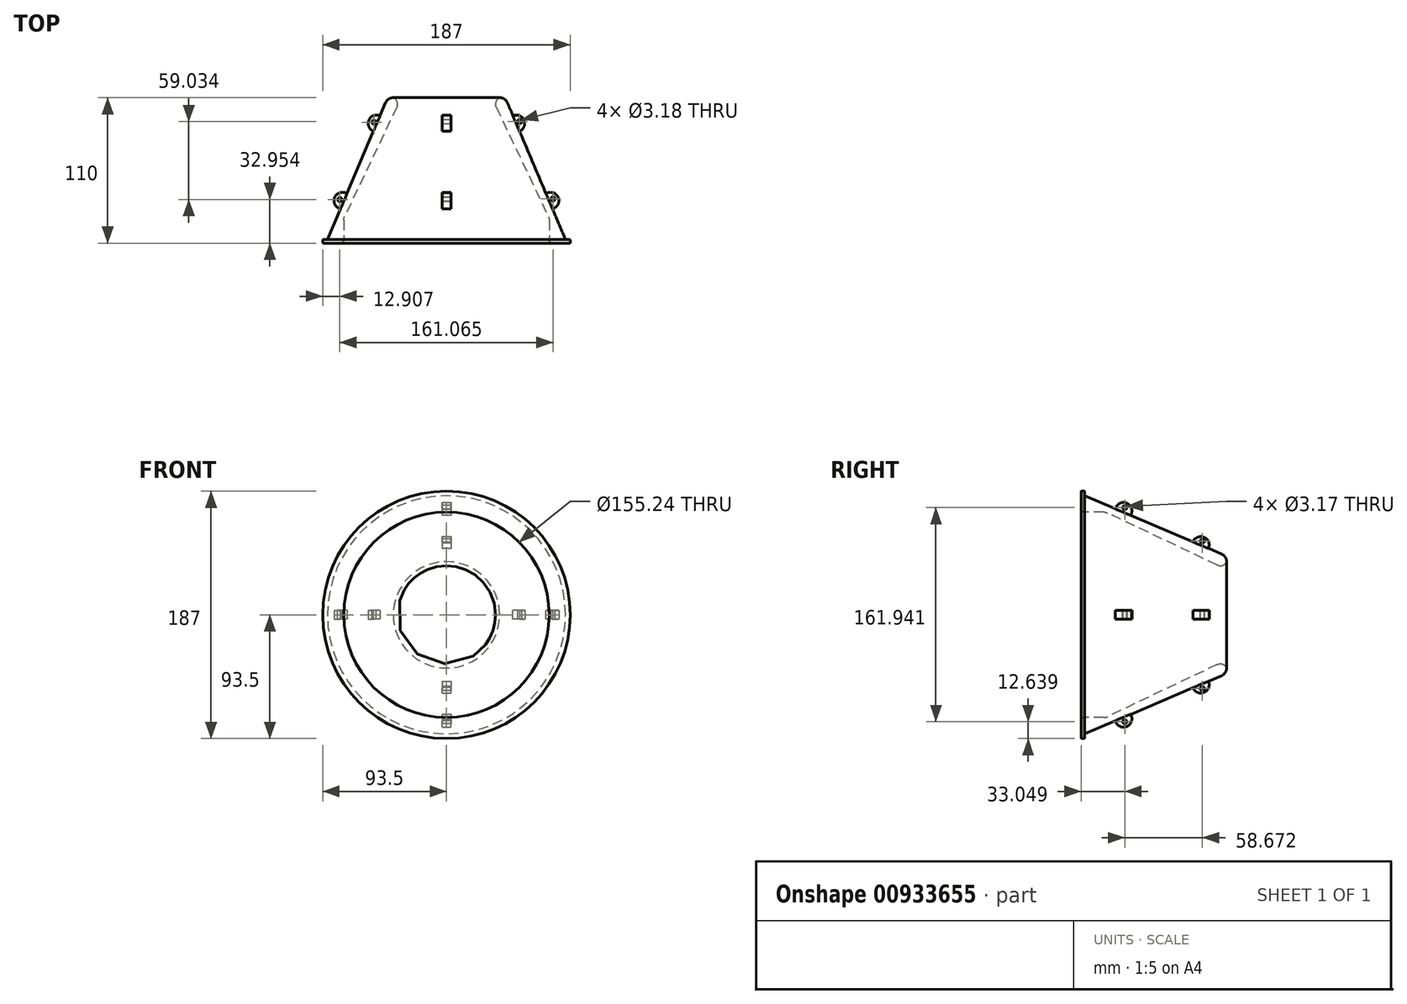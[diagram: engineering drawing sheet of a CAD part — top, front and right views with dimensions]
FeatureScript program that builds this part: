
annotation { "Feature Type Name" : "Feature", "Feature Type Description" : "" }
export const myFeature = defineFeature(function(context is Context, id is Id, definition is map)
    precondition{}
    {
        {
            var Q0;
            Q0=qCreatedBy(makeId("Top.planeOp"),FACE);
            var sketch = newSketch(context, id + "F0", { "sketchPlane" : qUnion([Q0])});
            skCircle(sketch, "E0", {"center": v(0, 0) * mm, "radius": 90 * mm});
            skSolve(sketch);
        }
        {
            var Q0;
            Q0=qCreatedBy(makeId("Top.planeOp"),FACE);
            var sketch = newSketch(context, id + "F1", { "sketchPlane" : qUnion([Q0])});
            skLineSegment(sketch, "E1", {"start": v(-77.62, 0) * mm, "end": v(-93.5, 0) * mm});
            skLineSegment(sketch, "E2", {"start": v(-93.5, 0) * mm, "end": v(-93.5, 2.72) * mm});
            skLineSegment(sketch, "E3", {"start": v(-93.5, 2.72) * mm, "end": v(-89.95, 2.72) * mm});
            skLineSegment(sketch, "E4", {"start": v(-93.5, 0) * mm, "end": v(-77.62, 0) * mm});
            skLineSegment(sketch, "E5", {"start": v(-37, 110) * mm, "end": v(-40.22, 110) * mm});
            skLineSegment(sketch, "E6", {"start": v(-46.07, 106.13) * mm, "end": v(-89.95, 2.72) * mm});
            skLineSegment(sketch, "E7", {"start": v(-77.62, 0) * mm, "end": v(-77.62, 17.26) * mm});
            skLineSegment(sketch, "E8", {"start": v(-37, 110) * mm, "end": v(-37, 105.53) * mm});
            skLineSegment(sketch, "E9", {"start": v(-37.62, 102.8) * mm, "end": v(-77, 20) * mm});
            skPoint(sketch, "E10.visualSharp", {"position": v(-37, 104.1) * mm});
            skArc(sketch, "E10.filletArc", {"start": v(-37.62, 102.8) * mm, "mid": v(-37.16, 104.13) * mm, "end": v(-37, 105.53) * mm});
            skPoint(sketch, "E11.visualSharp", {"position": v(-44.43, 110) * mm});
            skArc(sketch, "E11.filletArc", {"start": v(-40.22, 110) * mm, "mid": v(-43.73, 108.94) * mm, "end": v(-46.07, 106.13) * mm});
            skPoint(sketch, "E12.visualSharp", {"position": v(-77.62, 18.7) * mm});
            skArc(sketch, "E12.filletArc", {"start": v(-77, 20) * mm, "mid": v(-77.46, 18.66) * mm, "end": v(-77.62, 17.26) * mm});
            skLineSegment(sketch, "E13", {"start": v(0, 0) * mm, "end": v(0, 56.66) * mm});
            skSolve(sketch);
        }
        {
            var Q0;
            Q0=makeQuery(id+"F1.imprint","IMPRINT",FACE,{"disambiguationData":[TD([[makeQuery(id+"F1.imprint","IMPRINT",EDGE,{"derivedFrom":sQuery(id+"F1.wireOp",EDGE,"E2")}),-1.0]])]});
            var Q1;
            Q1=sQuery(id+"F1.wireOp",EDGE,"E13");
            revolve(context, id + "F2", {"surfaceOperationType" : NewSurfaceOperationType.NEW, "entities" : qUnion([Q0]), "axis" : qUnion([Q1]), "revolveType" : RevolveType.FULL});
        }
        {
            var Q0;
            Q0=makeQuery(id+"F2.opRevolve","SWEPT_EDGE",EDGE,{"disambiguationData":[OSD([sQuery(id+"F1.wireOp",EDGE,"E5"),sQuery(id+"F1.wireOp",EDGE,"E8")])]});
            fillet(context, id + "F3", {"entities" : qUnion([Q0]), "radius" : 5.08 * mm, "tangentPropagation" : true, "allowEdgeOverflow" : false});
        }
        {
            var Q0;
            Q0=makeQuery(id+"F2.opRevolve","SWEPT_EDGE",EDGE,{"disambiguationData":[OSD([sQuery(id+"F1.wireOp",EDGE,"E4"),sQuery(id+"F1.wireOp",EDGE,"E7")])]});
            fillet(context, id + "F4", {"entities" : qUnion([Q0]), "radius" : 2.54 * mm, "tangentPropagation" : true, "allowEdgeOverflow" : false});
        }
        {
            var Q0;
            Q0=makeQuery(id+"F2.opRevolve","SWEPT_EDGE",EDGE,{"disambiguationData":[OSD([sQuery(id+"F1.wireOp",EDGE,"E2"),sQuery(id+"F1.wireOp",EDGE,"E3")])]});
            var Q1;
            Q1=makeQuery(id+"F2.opRevolve","SWEPT_EDGE",EDGE,{"disambiguationData":[OSD([sQuery(id+"F1.wireOp",EDGE,"E2"),sQuery(id+"F1.wireOp",EDGE,"E4")])]});
            fillet(context, id + "F5", {"entities" : qUnion([Q0, Q1]), "radius" : 0.5 * mm, "tangentPropagation" : true, "allowEdgeOverflow" : false});
        }
        {
            var Q0;
            Q0=qCreatedBy(makeId("Top.planeOp"),FACE);
            var sketch = newSketch(context, id + "F6", { "sketchPlane" : qUnion([Q0])});
            skCircle(sketch, "E14", {"center": v(-78.58, 32.1) * mm, "radius": 6.35 * mm});
            skCircle(sketch, "E15", {"center": v(-52.78, 90.51) * mm, "radius": 6.35 * mm});
            skCircle(sketch, "E16.MirrorC", {"center": v(52.78, 90.51) * mm, "radius": 6.35 * mm});
            skCircle(sketch, "E17.MirrorC", {"center": v(78.58, 32.1) * mm, "radius": 6.35 * mm});
            skSolve(sketch);
        }
        {
            var Q0;
            Q0 = qSketchRegion(id + "F6", true);
            extrude(context, id + "F7", {"entities" : qUnion([Q0]), "operationType" : NewBodyOperationType.ADD, "endBound" : BoundingType.SYMMETRIC, "depth" : 6.6 * mm, "offsetDistance" : 25.4 * mm});
        }
        {
            var Q0;
            Q0=makeQuery(id+"F2.opRevolve","SWEPT_BODY",BODY,{"disambiguationData":[OSD([sQuery(id+"F1.wireOp",EDGE,"E2"),sQuery(id+"F1.wireOp",EDGE,"E3"),sQuery(id+"F1.wireOp",EDGE,"E4"),sQuery(id+"F1.wireOp",EDGE,"E5"),sQuery(id+"F1.wireOp",EDGE,"E6"),sQuery(id+"F1.wireOp",EDGE,"E7"),sQuery(id+"F1.wireOp",EDGE,"E8"),sQuery(id+"F1.wireOp",EDGE,"E9"),sQuery(id+"F1.wireOp",EDGE,"E10.filletArc"),sQuery(id+"F1.wireOp",EDGE,"E11.filletArc"),sQuery(id+"F1.wireOp",EDGE,"E12.filletArc")])]});
            var Q1;
            Q1=sQuery(id+"F1.wireOp",EDGE,"E13");
            transform(context, id + "F8", {"entities" : qUnion([Q0]), "transformType" : TransformType.ROTATION, "transformAxis" : qUnion([Q1]), "angle" : 90 * degree, "oppositeDirection" : true, "makeCopy" : false});
        }
        {
            var Q0;
            Q0 = qSketchRegion(id + "F6", true);
            extrude(context, id + "F9", {"entities" : qUnion([Q0]), "operationType" : NewBodyOperationType.ADD, "endBound" : BoundingType.SYMMETRIC, "depth" : 6.6 * mm, "offsetDistance" : 25.4 * mm});
        }
        {
            var Q0;
            Q0=makeQuery(id+"F9.opExtrude","CAP_FACE",FACE,{"disambiguationData":[OSD([sQuery(id+"F6.wireOp",EDGE,"E16.MirrorC")])],"isStart":true});
            var sketch = newSketch(context, id + "F10", { "sketchPlane" : qUnion([Q0])});
            skCircle(sketch, "E18", {"center": v(55.32, -91.99) * mm, "radius": 1.59 * mm});
            skCircle(sketch, "E19", {"center": v(80.47, -33.45) * mm, "radius": 1.59 * mm});
            skCircle(sketch, "E20", {"center": v(-80.6, -32.95) * mm, "radius": 1.59 * mm});
            skCircle(sketch, "E21", {"center": v(-54.84, -91.46) * mm, "radius": 1.59 * mm});
            skSolve(sketch);
        }
        {
            var Q0;
            Q0 = qSketchRegion(id + "F10", true);
            var Q1;
            Q1 = qConstructionFilter(qBodyType(qCreatedBy(id + "F10" ,EDGE), BodyType.WIRE), ConstructionObject.NO);
            extrude(context, id + "F11", {"entities" : qUnion([Q0]), "operationType" : NewBodyOperationType.REMOVE, "surfaceEntities" : qUnion([Q1]), "endBound" : BoundingType.SYMMETRIC, "depth" : 25.4 * mm, "offsetDistance" : 25.4 * mm});
        }
        {
            var Q0;
            Q0=qCreatedBy(makeId("Right.planeOp"),FACE);
            var sketch = newSketch(context, id + "F12", { "sketchPlane" : qUnion([Q0])});
            skCircle(sketch, "E22", {"center": v(33.08, 81.08) * mm, "radius": 1.59 * mm});
            skCircle(sketch, "E23", {"center": v(91.72, 55.83) * mm, "radius": 1.59 * mm});
            skCircle(sketch, "E24", {"center": v(91.67, -55.8) * mm, "radius": 1.59 * mm});
            skCircle(sketch, "E25", {"center": v(33.05, -80.86) * mm, "radius": 1.59 * mm});
            skSolve(sketch);
        }
        {
            var Q0;
            Q0 = qSketchRegion(id + "F12", true);
            extrude(context, id + "F13", {"entities" : qUnion([Q0]), "operationType" : NewBodyOperationType.REMOVE, "endBound" : BoundingType.SYMMETRIC, "depth" : 25.4 * mm, "offsetDistance" : 25.4 * mm});
        }
    });
